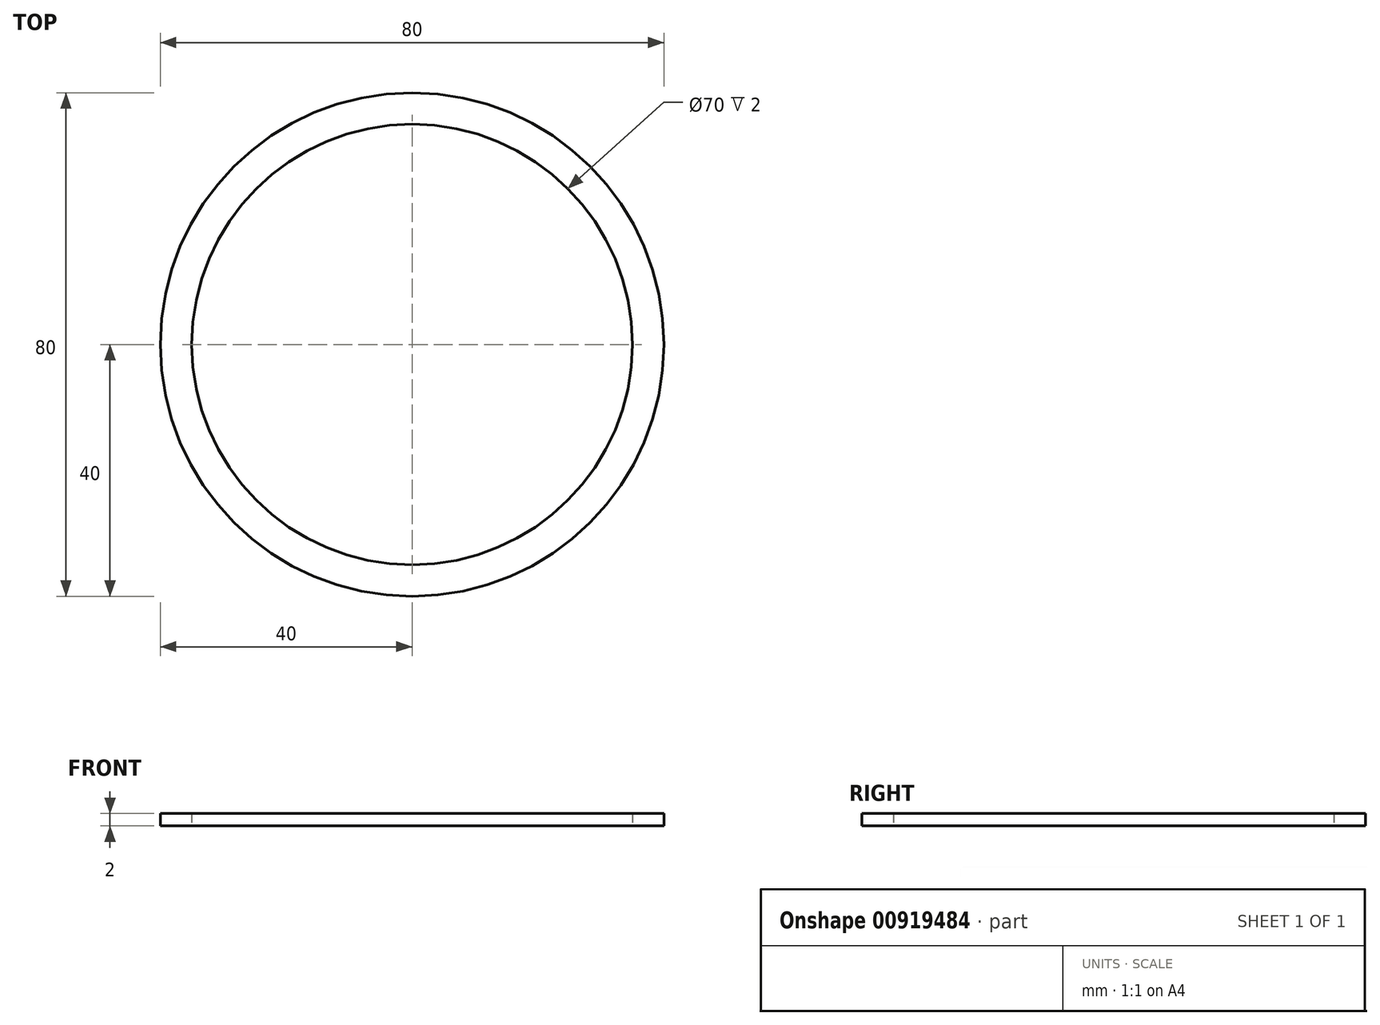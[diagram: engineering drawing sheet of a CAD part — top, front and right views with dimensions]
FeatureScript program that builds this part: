
annotation { "Feature Type Name" : "Feature", "Feature Type Description" : "" }
export const myFeature = defineFeature(function(context is Context, id is Id, definition is map)
    precondition{}
    {
        {
            var Q0;
            Q0=qCreatedBy(makeId("Top.planeOp"),FACE);
            var sketch = newSketch(context, id + "F0", { "sketchPlane" : qUnion([Q0])});
            skCircle(sketch, "E0", {"center": v(0, 0) * mm, "radius": 40 * mm});
            skCircle(sketch, "E1.0", {"center": v(0, 0) * mm, "radius": 35 * mm});
            skSolve(sketch);
        }
        {
            var Q0;
            Q0=qSketchRegion(id+"F0",true);
            extrude(context, id + "F1", {"entities" : qUnion([Q0]), "depth" : 2 * mm, "offsetDistance" : 25 * mm});
        }
    });
